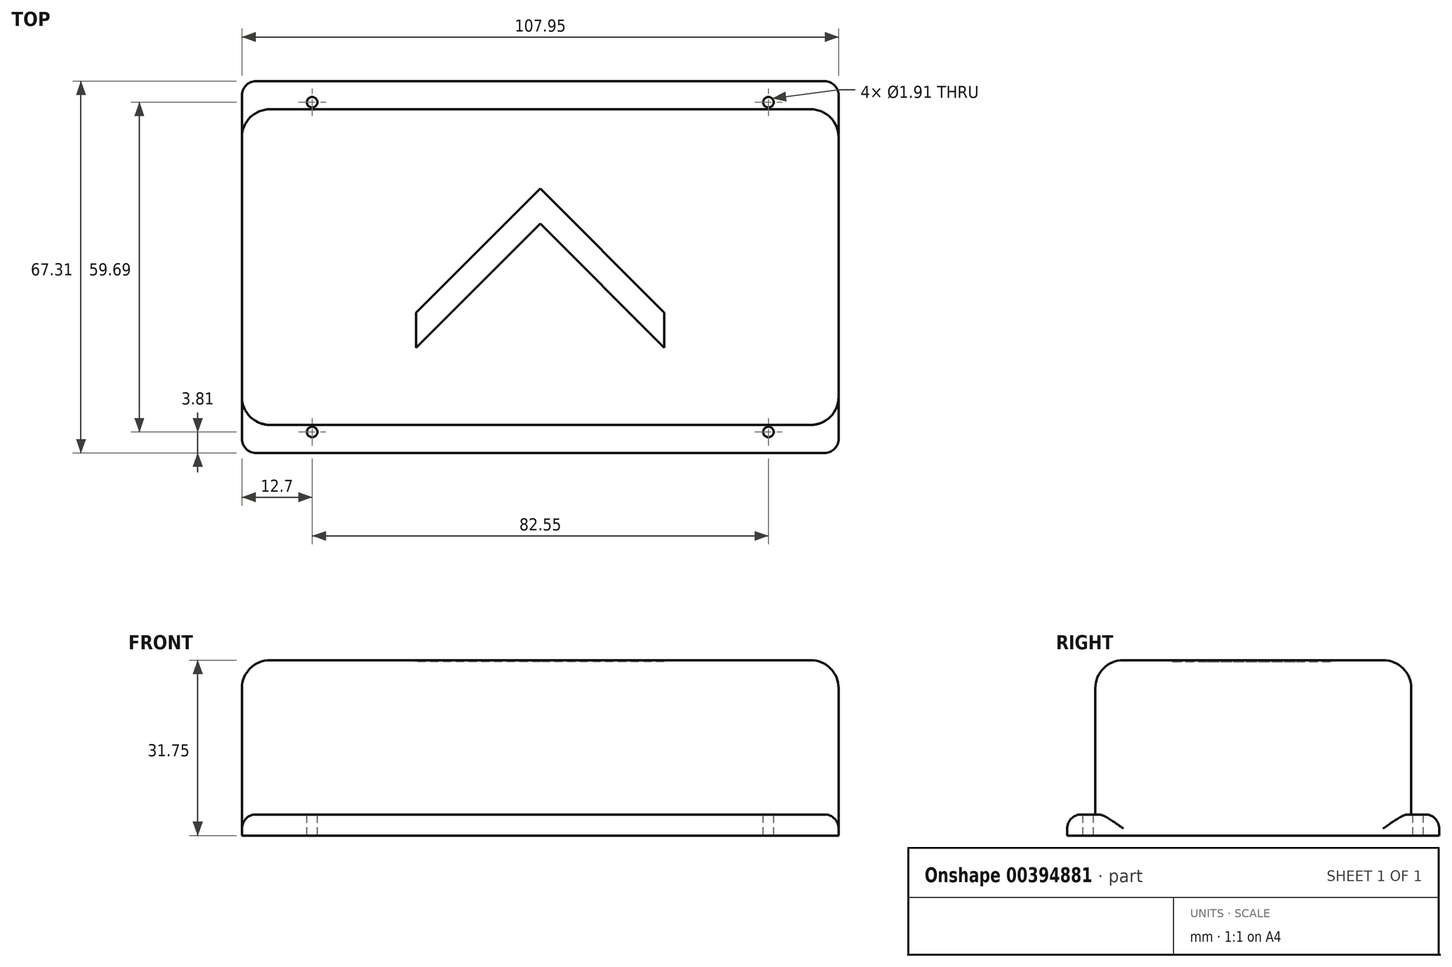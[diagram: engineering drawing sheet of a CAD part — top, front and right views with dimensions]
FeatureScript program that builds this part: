
annotation { "Feature Type Name" : "Feature", "Feature Type Description" : "" }
export const myFeature = defineFeature(function(context is Context, id is Id, definition is map)
    precondition{}
    {
        {
            var Q0;
            Q0=qCreatedBy(makeId("Top.planeOp"),FACE);
            var sketch = newSketch(context, id + "F0", { "sketchPlane" : qUnion([Q0])});
            skLineSegment(sketch, "E0.bottom", {"start": v(0, 0) * mm, "end": v(-107.95, 0) * mm});
            skLineSegment(sketch, "E0.top", {"start": v(0, -57.15) * mm, "end": v(-107.95, -57.15) * mm});
            skLineSegment(sketch, "E0.left", {"start": v(0, 0) * mm, "end": v(0, -57.15) * mm});
            skLineSegment(sketch, "E0.right", {"start": v(-107.95, 0) * mm, "end": v(-107.95, -57.15) * mm});
            skLineSegment(sketch, "E1.bottom", {"start": v(-53.98, 0) * mm, "end": v(-53.98, 0) * mm});
            skSolve(sketch);
        }
        {
            var Q0;
            Q0 = qSketchRegion(id + "F0", true);
            extrude(context, id + "F1", {"entities" : qUnion([Q0]), "oppositeDirection" : true, "depth" : 31.75 * mm});
        }
        {
            var Q0;
            Q0=makeQuery(id+"F1.opExtrude","SWEPT_FACE",FACE,{"disambiguationData":[OSD([sQuery(id+"F0.wireOp",EDGE,"E0.top")])]});
            var sketch = newSketch(context, id + "F2", { "sketchPlane" : qUnion([Q0])});
            skLineSegment(sketch, "E2.bottom", {"start": v(-107.95, -31.75) * mm, "end": v(0, -31.75) * mm});
            skLineSegment(sketch, "E2.top", {"start": v(-107.95, -27.94) * mm, "end": v(0, -27.94) * mm});
            skLineSegment(sketch, "E2.left", {"start": v(-107.95, -31.75) * mm, "end": v(-107.95, -27.94) * mm});
            skLineSegment(sketch, "E2.right", {"start": v(0, -31.75) * mm, "end": v(0, -27.94) * mm});
            skSolve(sketch);
        }
        {
            var Q0;
            Q0 = qSketchRegion(id + "F2", true);
            extrude(context, id + "F3", {"entities" : qUnion([Q0]), "operationType" : NewBodyOperationType.ADD, "depth" : 5.08 * mm});
        }
        {
            var Q0;
            Q0=makeQuery(id+"F1.opExtrude","SWEPT_FACE",FACE,{"disambiguationData":[OSD([sQuery(id+"F0.wireOp",EDGE,"E0.bottom")])]});
            var sketch = newSketch(context, id + "F4", { "sketchPlane" : qUnion([Q0])});
            skLineSegment(sketch, "E3.bottom", {"start": v(0, -31.75) * mm, "end": v(107.95, -31.75) * mm});
            skLineSegment(sketch, "E3.top", {"start": v(0, -27.94) * mm, "end": v(107.95, -27.94) * mm});
            skLineSegment(sketch, "E3.left", {"start": v(0, -31.75) * mm, "end": v(0, -27.94) * mm});
            skLineSegment(sketch, "E3.right", {"start": v(107.95, -31.75) * mm, "end": v(107.95, -27.94) * mm});
            skSolve(sketch);
        }
        {
            var Q0;
            Q0 = qSketchRegion(id + "F4", true);
            extrude(context, id + "F5", {"entities" : qUnion([Q0]), "operationType" : NewBodyOperationType.ADD, "depth" : 5.08 * mm});
        }
        {
            var Q0;
            Q0=makeQuery(id+"F3.opExtrude","SWEPT_FACE",FACE,{"disambiguationData":[OSD([sQuery(id+"F2.wireOp",EDGE,"E2.top")])]});
            var sketch = newSketch(context, id + "F6", { "sketchPlane" : qUnion([Q0])});
            skCircle(sketch, "E4", {"center": v(-12.7, -58.42) * mm, "radius": 0.95 * mm});
            skCircle(sketch, "E5", {"center": v(-95.25, -58.42) * mm, "radius": 0.95 * mm});
            skCircle(sketch, "E6", {"center": v(-95.25, 1.27) * mm, "radius": 0.95 * mm});
            skCircle(sketch, "E7", {"center": v(-12.7, 1.27) * mm, "radius": 0.95 * mm});
            skSolve(sketch);
        }
        {
            var Q0;
            Q0 = qSketchRegion(id + "F6", true);
            extrude(context, id + "F7", {"entities" : qUnion([Q0]), "operationType" : NewBodyOperationType.REMOVE, "oppositeDirection" : true, "depth" : 3.8 * mm});
        }
        {
            var Q0;
            Q0=makeQuery(id+"F1.opExtrude","CAP_EDGE",EDGE,{"disambiguationData":[OSD([sQuery(id+"F0.wireOp",EDGE,"E0.bottom")])],"isStart":true});
            var Q1;
            Q1=makeQuery(id+"F1.opExtrude","CAP_EDGE",EDGE,{"disambiguationData":[OSD([sQuery(id+"F0.wireOp",EDGE,"E0.top")])],"isStart":true});
            var Q2;
            Q2=makeQuery(id+"F1.opExtrude","CAP_EDGE",EDGE,{"disambiguationData":[OSD([sQuery(id+"F0.wireOp",EDGE,"E0.right")])],"isStart":true});
            var Q3;
            Q3=makeQuery(id+"F1.opExtrude","CAP_EDGE",EDGE,{"disambiguationData":[OSD([sQuery(id+"F0.wireOp",EDGE,"E0.left")])],"isStart":true});
            var Q4;
            Q4=makeQuery(id+"F1.opExtrude","SWEPT_EDGE",EDGE,{"disambiguationData":[OSD([sQuery(id+"F0.wireOp",EDGE,"E0.top"),sQuery(id+"F0.wireOp",EDGE,"E0.left")])]});
            var Q5;
            Q5=makeQuery(id+"F1.opExtrude","SWEPT_EDGE",EDGE,{"disambiguationData":[OSD([sQuery(id+"F0.wireOp",EDGE,"E0.top"),sQuery(id+"F0.wireOp",EDGE,"E0.right")])]});
            var Q6;
            Q6=makeQuery(id+"F1.opExtrude","SWEPT_EDGE",EDGE,{"disambiguationData":[OSD([sQuery(id+"F0.wireOp",EDGE,"E0.bottom"),sQuery(id+"F0.wireOp",EDGE,"E0.right")])]});
            var Q7;
            Q7=makeQuery(id+"F1.opExtrude","SWEPT_EDGE",EDGE,{"disambiguationData":[OSD([sQuery(id+"F0.wireOp",EDGE,"E0.bottom"),sQuery(id+"F0.wireOp",EDGE,"E0.left")])]});
            fillet(context, id + "F8", {"entities" : qUnion([Q0, Q1, Q2, Q3, Q4, Q5, Q6, Q7]), "radius" : 5.08 * mm, "tangentPropagation" : true, "allowEdgeOverflow" : false});
        }
        {
            var Q0;
            Q0=makeQuery(id+"F3.opExtrude","SWEPT_EDGE",EDGE,{"disambiguationData":[OSD([sQuery(id+"F0.wireOp",EDGE,"E0.top"),sQuery(id+"F0.wireOp",EDGE,"E0.right"),sQuery(id+"F2.wireOp",EDGE,"E2.top"),sQuery(id+"F2.wireOp",EDGE,"E2.left")])]});
            var Q1;
            Q1=makeQuery(id+"F3.opExtrude","CAP_EDGE",EDGE,{"disambiguationData":[OSD([sQuery(id+"F2.wireOp",EDGE,"E2.top")])],"isStart":false});
            var Q2;
            Q2=makeQuery(id+"F3.opExtrude","SWEPT_EDGE",EDGE,{"disambiguationData":[OSD([sQuery(id+"F0.wireOp",EDGE,"E0.top"),sQuery(id+"F0.wireOp",EDGE,"E0.left"),sQuery(id+"F2.wireOp",EDGE,"E2.top"),sQuery(id+"F2.wireOp",EDGE,"E2.right")])]});
            var Q3;
            Q3=makeQuery(id+"F5.opExtrude","SWEPT_EDGE",EDGE,{"disambiguationData":[OSD([sQuery(id+"F0.wireOp",EDGE,"E0.bottom"),sQuery(id+"F0.wireOp",EDGE,"E0.right"),sQuery(id+"F4.wireOp",EDGE,"E3.top"),sQuery(id+"F4.wireOp",EDGE,"E3.right")])]});
            var Q4;
            Q4=makeQuery(id+"F5.opExtrude","CAP_EDGE",EDGE,{"disambiguationData":[OSD([sQuery(id+"F4.wireOp",EDGE,"E3.top")])],"isStart":false});
            var Q5;
            Q5=makeQuery(id+"F5.opExtrude","SWEPT_EDGE",EDGE,{"disambiguationData":[OSD([sQuery(id+"F0.wireOp",EDGE,"E0.bottom"),sQuery(id+"F0.wireOp",EDGE,"E0.left"),sQuery(id+"F4.wireOp",EDGE,"E3.top"),sQuery(id+"F4.wireOp",EDGE,"E3.left")])]});
            fillet(context, id + "F9", {"entities" : qUnion([Q0, Q1, Q2, Q3, Q4, Q5]), "radius" : 2.54 * mm, "tangentPropagation" : true, "allowEdgeOverflow" : false});
        }
        {
            var Q0;
            {var subQ0=sQuery(id+"F2.wireOp",EDGE,"E2.top");Q0=makeQuery(id+"F9.opFillet","BLEND_EDGE",EDGE,{"blendedFrom":[makeQuery(id+"F3.opExtrude","CAP_EDGE",EDGE,{"disambiguationData":[OSD([subQ0])],"isStart":false}),makeQuery(id+"F3.opExtrude","SWEPT_EDGE",EDGE,{"disambiguationData":[OSD([sQuery(id+"F0.wireOp",EDGE,"E0.top"),sQuery(id+"F0.wireOp",EDGE,"E0.left"),subQ0,sQuery(id+"F2.wireOp",EDGE,"E2.right")])]})],"blendedInto":[]});}
            var Q1;
            {var subQ0=sQuery(id+"F2.wireOp",EDGE,"E2.top");Q1=makeQuery(id+"F9.opFillet","BLEND_EDGE",EDGE,{"blendedFrom":[makeQuery(id+"F3.opExtrude","CAP_EDGE",EDGE,{"disambiguationData":[OSD([subQ0])],"isStart":false}),makeQuery(id+"F3.opExtrude","SWEPT_EDGE",EDGE,{"disambiguationData":[OSD([sQuery(id+"F0.wireOp",EDGE,"E0.top"),sQuery(id+"F0.wireOp",EDGE,"E0.right"),subQ0,sQuery(id+"F2.wireOp",EDGE,"E2.left")])]})],"blendedInto":[]});}
            var Q2;
            {var subQ0=sQuery(id+"F4.wireOp",EDGE,"E3.top");Q2=makeQuery(id+"F9.opFillet","BLEND_EDGE",EDGE,{"blendedFrom":[makeQuery(id+"F5.opExtrude","CAP_EDGE",EDGE,{"disambiguationData":[OSD([subQ0])],"isStart":false}),makeQuery(id+"F5.opExtrude","SWEPT_EDGE",EDGE,{"disambiguationData":[OSD([sQuery(id+"F0.wireOp",EDGE,"E0.bottom"),sQuery(id+"F0.wireOp",EDGE,"E0.right"),subQ0,sQuery(id+"F4.wireOp",EDGE,"E3.right")])]})],"blendedInto":[]});}
            var Q3;
            {var subQ0=sQuery(id+"F4.wireOp",EDGE,"E3.top");Q3=makeQuery(id+"F9.opFillet","BLEND_EDGE",EDGE,{"blendedFrom":[makeQuery(id+"F5.opExtrude","CAP_EDGE",EDGE,{"disambiguationData":[OSD([subQ0])],"isStart":false}),makeQuery(id+"F5.opExtrude","SWEPT_EDGE",EDGE,{"disambiguationData":[OSD([sQuery(id+"F0.wireOp",EDGE,"E0.bottom"),sQuery(id+"F0.wireOp",EDGE,"E0.left"),subQ0,sQuery(id+"F4.wireOp",EDGE,"E3.left")])]})],"blendedInto":[]});}
            fillet(context, id + "F10", {"entities" : qUnion([Q0, Q1, Q2, Q3]), "radius" : 2.54 * mm, "tangentPropagation" : true, "allowEdgeOverflow" : false});
        }
        {
            var Q0;
            Q0=makeQuery(id+"F1.opExtrude","CAP_FACE",FACE,{"disambiguationData":[OSD([sQuery(id+"F0.wireOp",EDGE,"E0.bottom"),sQuery(id+"F0.wireOp",EDGE,"E0.top"),sQuery(id+"F0.wireOp",EDGE,"E0.left"),sQuery(id+"F0.wireOp",EDGE,"E0.right")])],"isStart":true});
            var sketch = newSketch(context, id + "F11", { "sketchPlane" : qUnion([Q0])});
            skLineSegment(sketch, "E8", {"start": v(-53.98, -14.37) * mm, "end": v(-76.43, -36.82) * mm});
            skLineSegment(sketch, "E9", {"start": v(-76.43, -36.82) * mm, "end": v(-76.43, -43.17) * mm});
            skLineSegment(sketch, "E10", {"start": v(-76.43, -43.17) * mm, "end": v(-53.98, -20.72) * mm});
            skLineSegment(sketch, "E11", {"start": v(-53.98, -20.72) * mm, "end": v(-31.52, -43.17) * mm});
            skLineSegment(sketch, "E12", {"start": v(-31.52, -43.17) * mm, "end": v(-31.52, -36.82) * mm});
            skLineSegment(sketch, "E13", {"start": v(-31.52, -36.82) * mm, "end": v(-53.98, -14.37) * mm});
            skSolve(sketch);
        }
        {
            var Q0;
            Q0 = qSketchRegion(id + "F11", true);
            extrude(context, id + "F12", {"entities" : qUnion([Q0]), "operationType" : NewBodyOperationType.REMOVE, "oppositeDirection" : true, "depth" : 0.25 * mm});
        }
    });
